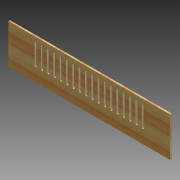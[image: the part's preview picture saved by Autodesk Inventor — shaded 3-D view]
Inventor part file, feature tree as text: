
AUTODESK INVENTOR PART (.ipt)
format: ipt  version: 2012 (Build 160160000, 160)  size: 229,888 bytes
history: native  units: in
note: dims shown in document units (in); Inventor stores cm internally (conversion verified against a paired STEP export)
features: extrude x1, fillet x1, sketch x1
ambient origin geometry x8: Origin, YZ Plane, XZ Plane, XY Plane, X Axis, Y Axis, Z Axis, Center Point
bodies: Solid1 (feature_tree)
feature tree (3):
  extrude  "Extrusion1"  Depth=9.0in
  fillet  "Fillet1"  Radius=0.375in
  sketch  "Sketch1"  dims[d0=37.0in d1=9.0in d2=0.375in d3=0.0in d4=6.0in d5=18.25in d6=0.5in d7=5.0in d9=0.25in d10=1.0in d11=7.0866in d13=1.4412in d14=0.3937in d16=1.0in]
